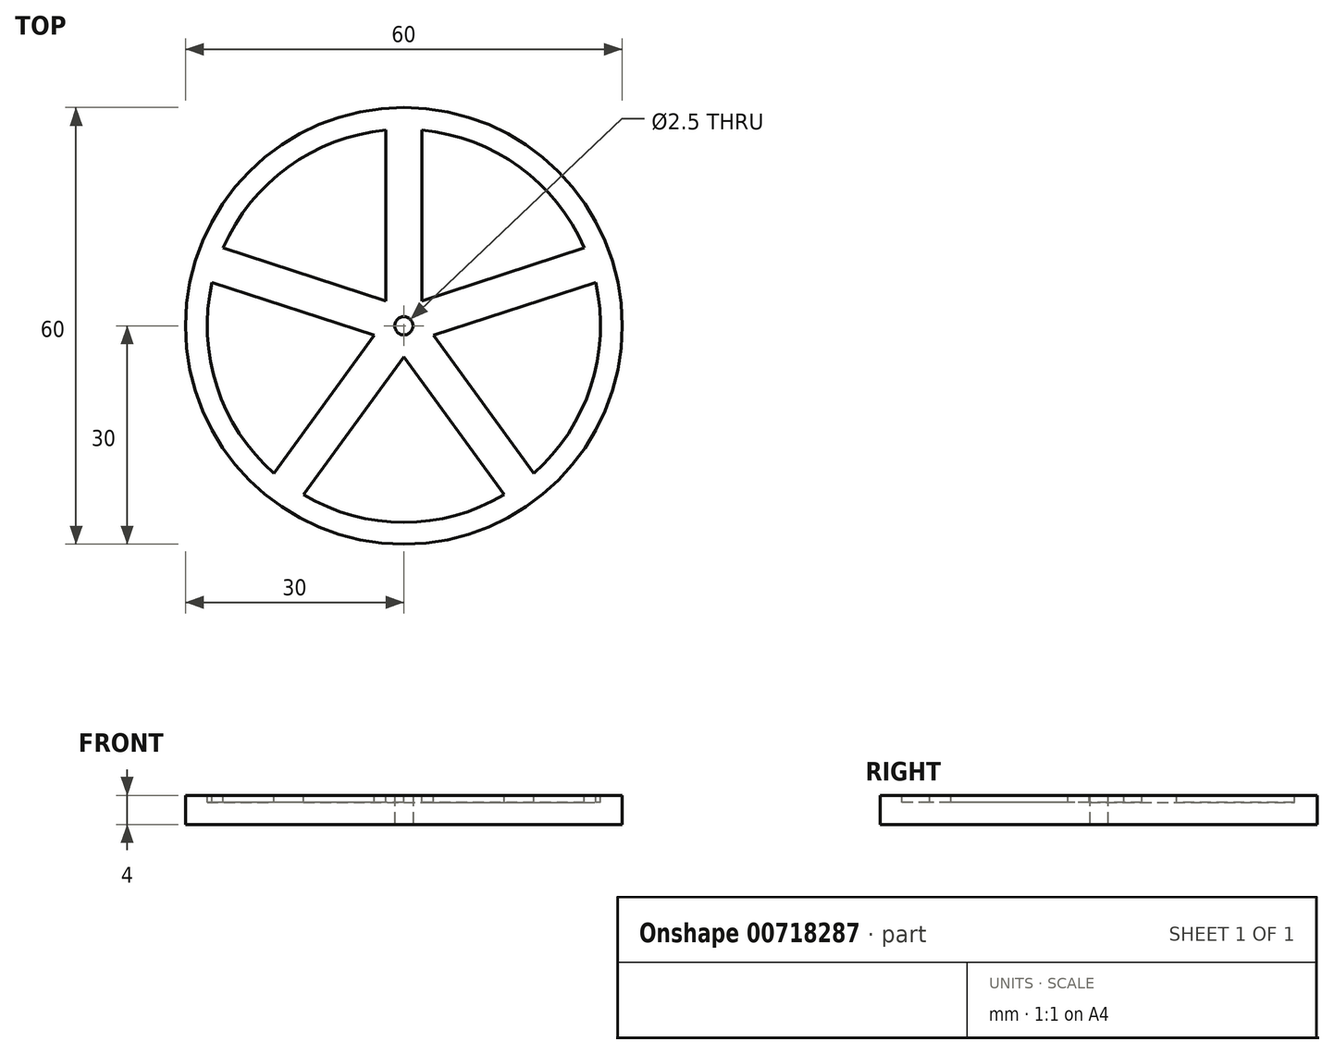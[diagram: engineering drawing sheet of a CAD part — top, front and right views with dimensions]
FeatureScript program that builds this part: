
annotation { "Feature Type Name" : "Feature", "Feature Type Description" : "" }
export const myFeature = defineFeature(function(context is Context, id is Id, definition is map)
    precondition{}
    {
        {
            var Q0;
            Q0=qCreatedBy(makeId("Top.planeOp"),FACE);
            var sketch = newSketch(context, id + "F0", { "sketchPlane" : qUnion([Q0])});
            skCircle(sketch, "E0", {"center": v(0, 0) * mm, "radius": 20 * mm, "construction": true});
            skLineSegment(sketch, "E1", {"start": v(0, 0) * mm, "end": v(0, 20) * mm, "construction": true});
            skLineSegment(sketch, "E2", {"start": v(0, 0) * mm, "end": v(10, 17.32) * mm, "construction": true});
            skCircle(sketch, "E3", {"center": v(0, 0) * mm, "radius": 30 * mm});
            skLineSegment(sketch, "E4", {"start": v(0, 0) * mm, "end": v(7.76, 28.98) * mm, "construction": true});
            skLineSegment(sketch, "E5", {"start": v(0, 20) * mm, "end": v(7.76, 28.98) * mm});
            skLineSegment(sketch, "E6", {"start": v(7.76, 28.98) * mm, "end": v(10, 17.32) * mm});
            skLineSegment(sketch, "E7.1.0", {"start": v(-10, 17.32) * mm, "end": v(-7.76, 28.98) * mm});
            skLineSegment(sketch, "E7.1.1", {"start": v(-7.76, 28.98) * mm, "end": v(0, 20) * mm});
            skLineSegment(sketch, "E7.2.0", {"start": v(-17.32, 10) * mm, "end": v(-21.21, 21.21) * mm});
            skLineSegment(sketch, "E7.2.1", {"start": v(-21.21, 21.21) * mm, "end": v(-10, 17.32) * mm});
            skLineSegment(sketch, "E7.3.0", {"start": v(-20, 0) * mm, "end": v(-28.98, 7.76) * mm});
            skLineSegment(sketch, "E7.3.1", {"start": v(-28.98, 7.76) * mm, "end": v(-17.32, 10) * mm});
            skLineSegment(sketch, "E7.4.0", {"start": v(-17.32, -10) * mm, "end": v(-28.98, -7.76) * mm});
            skLineSegment(sketch, "E7.4.1", {"start": v(-28.98, -7.76) * mm, "end": v(-20, 0) * mm});
            skLineSegment(sketch, "E7.5.0", {"start": v(-10, -17.32) * mm, "end": v(-21.21, -21.21) * mm});
            skLineSegment(sketch, "E7.5.1", {"start": v(-21.21, -21.21) * mm, "end": v(-17.32, -10) * mm});
            skLineSegment(sketch, "E7.6.0", {"start": v(0, -20) * mm, "end": v(-7.76, -28.98) * mm});
            skLineSegment(sketch, "E7.6.1", {"start": v(-7.76, -28.98) * mm, "end": v(-10, -17.32) * mm});
            skLineSegment(sketch, "E7.7.0", {"start": v(10, -17.32) * mm, "end": v(7.76, -28.98) * mm});
            skLineSegment(sketch, "E7.7.1", {"start": v(7.76, -28.98) * mm, "end": v(0, -20) * mm});
            skLineSegment(sketch, "E7.8.0", {"start": v(17.32, -10) * mm, "end": v(21.21, -21.21) * mm});
            skLineSegment(sketch, "E7.8.1", {"start": v(21.21, -21.21) * mm, "end": v(10, -17.32) * mm});
            skLineSegment(sketch, "E7.9.0", {"start": v(20, 0) * mm, "end": v(28.98, -7.76) * mm});
            skLineSegment(sketch, "E7.9.1", {"start": v(28.98, -7.76) * mm, "end": v(17.32, -10) * mm});
            skLineSegment(sketch, "E7.10.0", {"start": v(17.32, 10) * mm, "end": v(28.98, 7.76) * mm});
            skLineSegment(sketch, "E7.10.1", {"start": v(28.98, 7.76) * mm, "end": v(20, 0) * mm});
            skLineSegment(sketch, "E7.11.0", {"start": v(10, 17.32) * mm, "end": v(21.21, 21.21) * mm});
            skLineSegment(sketch, "E7.11.1", {"start": v(21.21, 21.21) * mm, "end": v(17.32, 10) * mm});
            skCircle(sketch, "E8", {"center": v(0, 0) * mm, "radius": 1.25 * mm});
            skSolve(sketch);
        }
        {
            var Q0;
            Q0=makeQuery(id+"F0.imprint","IMPRINT",FACE,{"disambiguationData":[TD([[makeQuery(id+"F0.imprint","IMPRINT",EDGE,{"derivedFrom":sQuery(id+"F0.wireOp",EDGE,"E5")}),-1.0]])]});
            var Q1;
            {var subQ0=sQuery(id+"F0.wireOp",EDGE,"E7.3.0");Q1=makeQuery(id+"F0.imprint","IMPRINT",FACE,{"disambiguationData":[TD([[makeQuery(id+"F0.imprint","IMPRINT",EDGE,{"derivedFrom":subQ0}),1.0]])]});}
            var Q2;
            {var subQ0=sQuery(id+"F0.wireOp",EDGE,"E7.2.0");Q2=makeQuery(id+"F0.imprint","IMPRINT",FACE,{"disambiguationData":[TD([[makeQuery(id+"F0.imprint","IMPRINT",EDGE,{"derivedFrom":subQ0}),1.0]])]});}
            var Q3;
            {var subQ0=sQuery(id+"F0.wireOp",EDGE,"E7.1.0");Q3=makeQuery(id+"F0.imprint","IMPRINT",FACE,{"disambiguationData":[TD([[makeQuery(id+"F0.imprint","IMPRINT",EDGE,{"derivedFrom":subQ0}),1.0]])]});}
            var Q4;
            {var subQ0=sQuery(id+"F0.wireOp",EDGE,"E5");Q4=makeQuery(id+"F0.imprint","IMPRINT",FACE,{"disambiguationData":[TD([[makeQuery(id+"F0.imprint","IMPRINT",EDGE,{"derivedFrom":subQ0}),1.0]])]});}
            var Q5;
            {var subQ0=sQuery(id+"F0.wireOp",EDGE,"E6");Q5=makeQuery(id+"F0.imprint","IMPRINT",FACE,{"disambiguationData":[TD([[makeQuery(id+"F0.imprint","IMPRINT",EDGE,{"derivedFrom":subQ0}),1.0]])]});}
            var Q6;
            {var subQ0=sQuery(id+"F0.wireOp",EDGE,"E7.10.0");Q6=makeQuery(id+"F0.imprint","IMPRINT",FACE,{"disambiguationData":[TD([[makeQuery(id+"F0.imprint","IMPRINT",EDGE,{"derivedFrom":subQ0}),1.0]])]});}
            var Q7;
            {var subQ0=sQuery(id+"F0.wireOp",EDGE,"E7.9.0");Q7=makeQuery(id+"F0.imprint","IMPRINT",FACE,{"disambiguationData":[TD([[makeQuery(id+"F0.imprint","IMPRINT",EDGE,{"derivedFrom":subQ0}),1.0]])]});}
            var Q8;
            {var subQ0=sQuery(id+"F0.wireOp",EDGE,"E7.8.0");Q8=makeQuery(id+"F0.imprint","IMPRINT",FACE,{"disambiguationData":[TD([[makeQuery(id+"F0.imprint","IMPRINT",EDGE,{"derivedFrom":subQ0}),1.0]])]});}
            var Q9;
            {var subQ0=sQuery(id+"F0.wireOp",EDGE,"E7.7.0");Q9=makeQuery(id+"F0.imprint","IMPRINT",FACE,{"disambiguationData":[TD([[makeQuery(id+"F0.imprint","IMPRINT",EDGE,{"derivedFrom":subQ0}),1.0]])]});}
            var Q10;
            {var subQ0=sQuery(id+"F0.wireOp",EDGE,"E7.6.0");Q10=makeQuery(id+"F0.imprint","IMPRINT",FACE,{"disambiguationData":[TD([[makeQuery(id+"F0.imprint","IMPRINT",EDGE,{"derivedFrom":subQ0}),1.0]])]});}
            var Q11;
            {var subQ0=sQuery(id+"F0.wireOp",EDGE,"E7.5.0");Q11=makeQuery(id+"F0.imprint","IMPRINT",FACE,{"disambiguationData":[TD([[makeQuery(id+"F0.imprint","IMPRINT",EDGE,{"derivedFrom":subQ0}),1.0]])]});}
            var Q12;
            {var subQ0=sQuery(id+"F0.wireOp",EDGE,"E7.4.0");Q12=makeQuery(id+"F0.imprint","IMPRINT",FACE,{"disambiguationData":[TD([[makeQuery(id+"F0.imprint","IMPRINT",EDGE,{"derivedFrom":subQ0}),1.0]])]});}
            extrude(context, id + "F1", {"entities" : qUnion([Q0, Q1, Q2, Q3, Q4, Q5, Q6, Q7, Q8, Q9, Q10, Q11, Q12]), "depth" : 4 * mm, "offsetDistance" : 25 * mm});
        }
        {
            var Q0;
            Q0=makeQuery(id+"F1.opExtrude","CAP_FACE",FACE,{"disambiguationData":[OSD([sQuery(id+"F0.wireOp",EDGE,"E5"),sQuery(id+"F0.wireOp",EDGE,"E6"),sQuery(id+"F0.wireOp",EDGE,"E7.1.0"),sQuery(id+"F0.wireOp",EDGE,"E7.1.1"),sQuery(id+"F0.wireOp",EDGE,"E7.2.0"),sQuery(id+"F0.wireOp",EDGE,"E7.2.1"),sQuery(id+"F0.wireOp",EDGE,"E7.3.0"),sQuery(id+"F0.wireOp",EDGE,"E7.3.1"),sQuery(id+"F0.wireOp",EDGE,"E7.4.0"),sQuery(id+"F0.wireOp",EDGE,"E7.4.1"),sQuery(id+"F0.wireOp",EDGE,"E7.5.0"),sQuery(id+"F0.wireOp",EDGE,"E7.5.1"),sQuery(id+"F0.wireOp",EDGE,"E7.6.0"),sQuery(id+"F0.wireOp",EDGE,"E7.6.1"),sQuery(id+"F0.wireOp",EDGE,"E7.7.0"),sQuery(id+"F0.wireOp",EDGE,"E7.7.1"),sQuery(id+"F0.wireOp",EDGE,"E7.8.0"),sQuery(id+"F0.wireOp",EDGE,"E7.8.1"),sQuery(id+"F0.wireOp",EDGE,"E7.9.0"),sQuery(id+"F0.wireOp",EDGE,"E7.9.1"),sQuery(id+"F0.wireOp",EDGE,"E7.10.0"),sQuery(id+"F0.wireOp",EDGE,"E7.10.1"),sQuery(id+"F0.wireOp",EDGE,"E7.11.0"),sQuery(id+"F0.wireOp",EDGE,"E7.11.1"),sQuery(id+"F0.wireOp",EDGE,"E8")])],"isStart":false});
            var sketch = newSketch(context, id + "F2", { "sketchPlane" : qUnion([Q0])});
            skCircle(sketch, "E9.0", {"center": v(0, 0) * mm, "radius": 4.25 * mm});
            skCircle(sketch, "E10", {"center": v(0, 0) * mm, "radius": 27 * mm});
            skLineSegment(sketch, "E11", {"start": v(0, 0) * mm, "end": v(0, 27) * mm, "construction": true});
            skLineSegment(sketch, "E12", {"start": v(2.5, 3.44) * mm, "end": v(2.5, 26.88) * mm});
            skLineSegment(sketch, "E13", {"start": v(-2.5, 3.44) * mm, "end": v(-2.5, 26.88) * mm});
            skLineSegment(sketch, "E14.1.0", {"start": v(-4.04, -1.32) * mm, "end": v(-26.34, 5.93) * mm});
            skLineSegment(sketch, "E14.1.1", {"start": v(-2.5, 3.44) * mm, "end": v(-24.8, 10.69) * mm});
            skLineSegment(sketch, "E14.2.0", {"start": v(0, -4.25) * mm, "end": v(-13.78, -23.22) * mm});
            skLineSegment(sketch, "E14.2.1", {"start": v(-4.04, -1.31) * mm, "end": v(-17.82, -20.28) * mm});
            skLineSegment(sketch, "E14.3.0", {"start": v(4.04, -1.31) * mm, "end": v(17.82, -20.28) * mm});
            skLineSegment(sketch, "E14.3.1", {"start": v(0, -4.25) * mm, "end": v(13.78, -23.22) * mm});
            skLineSegment(sketch, "E14.4.0", {"start": v(2.5, 3.44) * mm, "end": v(24.8, 10.69) * mm});
            skLineSegment(sketch, "E14.4.1", {"start": v(4.04, -1.32) * mm, "end": v(26.34, 5.93) * mm});
            skSolve(sketch);
        }
        {
            var Q0;
            {var subQ0=sQuery(id+"F2.wireOp",EDGE,"E13");var subQ1=sQuery(id+"F2.wireOp",EDGE,"E10");var subQ2=makeQuery(id+"F2.imprint","INTERSECT",VERTEX,{"derivedFrom":[subQ1,subQ0]});Q0=makeQuery(id+"F2.imprint","IMPRINT",FACE,{"disambiguationData":[TD([[makeQuery(id+"F2.imprint","IMPRINT",EDGE,{"disambiguationData":[TD([[subQ2,-1.0]])],"derivedFrom":subQ1}),1.0]])]});}
            var Q1;
            {var subQ0=sQuery(id+"F2.wireOp",EDGE,"E12");var subQ1=sQuery(id+"F2.wireOp",EDGE,"E10");var subQ2=makeQuery(id+"F2.imprint","INTERSECT",VERTEX,{"derivedFrom":[subQ1,subQ0]});Q1=makeQuery(id+"F2.imprint","IMPRINT",FACE,{"disambiguationData":[TD([[makeQuery(id+"F2.imprint","IMPRINT",EDGE,{"disambiguationData":[TD([[subQ2,1.0]])],"derivedFrom":subQ1}),1.0]])]});}
            var Q2;
            {var subQ0=sQuery(id+"F2.wireOp",EDGE,"E14.3.0");var subQ1=sQuery(id+"F2.wireOp",EDGE,"E10");var subQ2=makeQuery(id+"F2.imprint","INTERSECT",VERTEX,{"derivedFrom":[subQ1,subQ0]});Q2=makeQuery(id+"F2.imprint","IMPRINT",FACE,{"disambiguationData":[TD([[makeQuery(id+"F2.imprint","IMPRINT",EDGE,{"disambiguationData":[TD([[subQ2,-1.0]])],"derivedFrom":subQ1}),1.0]])]});}
            var Q3;
            {var subQ0=sQuery(id+"F2.wireOp",EDGE,"E14.2.0");var subQ1=sQuery(id+"F2.wireOp",EDGE,"E10");var subQ2=makeQuery(id+"F2.imprint","INTERSECT",VERTEX,{"derivedFrom":[subQ1,subQ0]});Q3=makeQuery(id+"F2.imprint","IMPRINT",FACE,{"disambiguationData":[TD([[makeQuery(id+"F2.imprint","IMPRINT",EDGE,{"disambiguationData":[TD([[subQ2,-1.0]])],"derivedFrom":subQ1}),1.0]])]});}
            var Q4;
            {var subQ0=sQuery(id+"F2.wireOp",EDGE,"E14.1.0");var subQ1=sQuery(id+"F2.wireOp",EDGE,"E10");var subQ2=makeQuery(id+"F2.imprint","INTERSECT",VERTEX,{"derivedFrom":[subQ1,subQ0]});Q4=makeQuery(id+"F2.imprint","IMPRINT",FACE,{"disambiguationData":[TD([[makeQuery(id+"F2.imprint","IMPRINT",EDGE,{"disambiguationData":[TD([[subQ2,-1.0]])],"derivedFrom":subQ1}),1.0]])]});}
            extrude(context, id + "F3", {"entities" : qUnion([Q0, Q1, Q2, Q3, Q4]), "operationType" : NewBodyOperationType.REMOVE, "oppositeDirection" : true, "depth" : 1 * mm, "offsetDistance" : 25 * mm});
        }
    });
